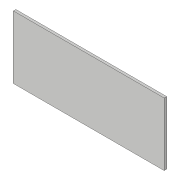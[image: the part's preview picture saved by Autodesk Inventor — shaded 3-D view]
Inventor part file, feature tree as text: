
AUTODESK INVENTOR PART (.ipt)
format: ipt  version: 2018 (Build 220112000, 112)  size: 86,528 bytes
history: native  units: in
note: dims shown in document units (in); Inventor stores cm internally (conversion verified against a paired STEP export)
features: extrude x1, sketch x1
ambient origin geometry x8: Origin, YZ Plane, XZ Plane, XY Plane, X Axis, Y Axis, Z Axis, Center Point
bodies: Body1 (feature_tree)
feature tree (2):
  extrude  "Extrusion1"  TaperAngle=90.0deg  [1 undecoded]
  sketch  "Sketch5"  dims[d3=9.8425in d4=90.0deg d5=23.622in d6=90.0deg d7=9.8425in d8=90.0deg d9=0.3937in d10=0.0in]
note: 1 required parameter value undecoded (feature->parameter linkage not recoverable at this tier; creation-order binding heuristic only, values carry confidence <= 0.55)
